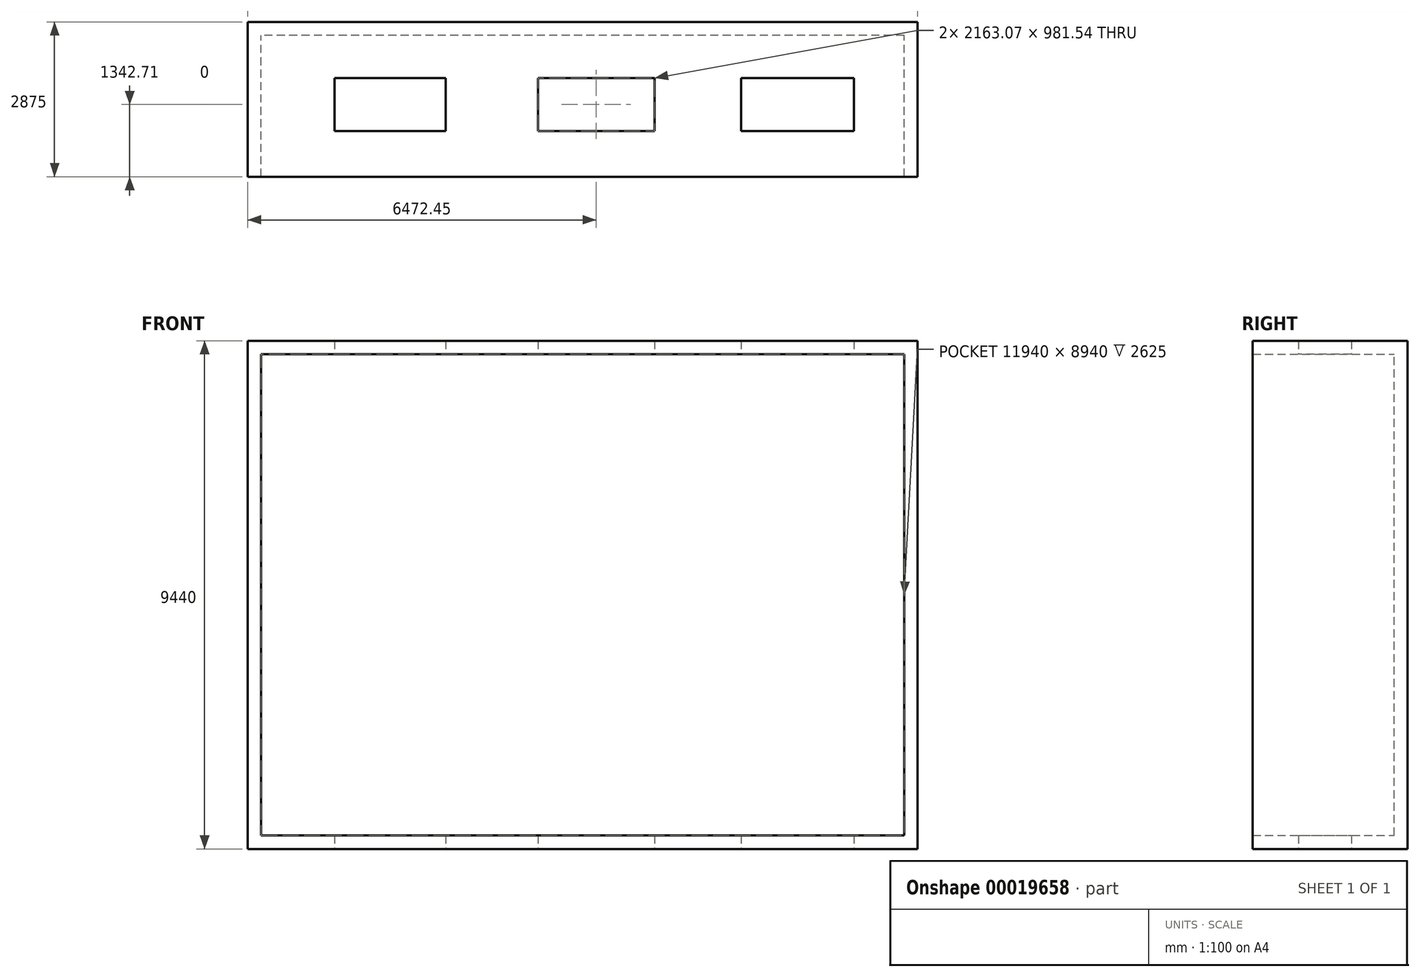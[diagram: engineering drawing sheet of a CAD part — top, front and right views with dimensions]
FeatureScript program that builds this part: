
annotation { "Feature Type Name" : "Feature", "Feature Type Description" : "" }
export const myFeature = defineFeature(function(context is Context, id is Id, definition is map)
    precondition{}
    {
        {
            var Q0;
            Q0=qCreatedBy(makeId("Front.planeOp"),FACE);
            var sketch = newSketch(context, id + "F0", { "sketchPlane" : qUnion([Q0])});
            skLineSegment(sketch, "E0.bottom", {"start": v(0, 0) * mm, "end": v(12440, 0) * mm});
            skLineSegment(sketch, "E0.top", {"start": v(0, 9440) * mm, "end": v(12440, 9440) * mm});
            skLineSegment(sketch, "E0.left", {"start": v(0, 0) * mm, "end": v(0, 9440) * mm});
            skLineSegment(sketch, "E0.right", {"start": v(12440, 0) * mm, "end": v(12440, 9440) * mm});
            skSolve(sketch);
        }
        {
            var Q0;
            Q0=makeQuery(id+"F0.imprint","IMPRINT",FACE,{"disambiguationData":[TD([[makeQuery(id+"F0.imprint","IMPRINT",EDGE,{"derivedFrom":sQuery(id+"F0.wireOp",EDGE,"E0.bottom")}),1.0]])]});
            extrude(context, id + "F1", {"entities" : qUnion([Q0]), "depth" : 250 * mm});
        }
        {
            var Q0;
            Q0=makeQuery(id+"F1.opExtrude","CAP_FACE",FACE,{"disambiguationData":[OSD([sQuery(id+"F0.wireOp",EDGE,"E0.bottom"),sQuery(id+"F0.wireOp",EDGE,"E0.top"),sQuery(id+"F0.wireOp",EDGE,"E0.left"),sQuery(id+"F0.wireOp",EDGE,"E0.right")])],"isStart":false});
            var sketch = newSketch(context, id + "F2", { "sketchPlane" : qUnion([Q0])});
            skLineSegment(sketch, "E1.0.0", {"start": v(0, 9440) * mm, "end": v(0, 0) * mm});
            skLineSegment(sketch, "E1.0.1", {"start": v(0, 0) * mm, "end": v(12440, 0) * mm});
            skLineSegment(sketch, "E1.0.2", {"start": v(12440, 0) * mm, "end": v(12440, 9440) * mm});
            skLineSegment(sketch, "E1.0.3", {"start": v(12440, 9440) * mm, "end": v(0, 9440) * mm});
            skLineSegment(sketch, "E2.0", {"start": v(12190, 9190) * mm, "end": v(250, 9190) * mm});
            skLineSegment(sketch, "E2.1", {"start": v(12190, 250) * mm, "end": v(12190, 9190) * mm});
            skLineSegment(sketch, "E2.2", {"start": v(250, 250) * mm, "end": v(12190, 250) * mm});
            skLineSegment(sketch, "E2.3", {"start": v(250, 9190) * mm, "end": v(250, 250) * mm});
            skSolve(sketch);
        }
        {
            var Q0;
            Q0=makeQuery(id+"F2.imprint","IMPRINT",FACE,{"disambiguationData":[TD([[makeQuery(id+"F2.imprint","IMPRINT",EDGE,{"derivedFrom":sQuery(id+"F2.wireOp",EDGE,"E1.0.0")}),-1.0]])]});
            extrude(context, id + "F3", {"entities" : qUnion([Q0]), "operationType" : NewBodyOperationType.ADD, "depth" : 2625 * mm});
        }
        {
            var Q0;
            Q0=makeQuery(id+"F3.boolean.opBoolean","MERGE",FACE,{"derivedFrom":[makeQuery(id+"F1.opExtrude","SWEPT_FACE",FACE,{"disambiguationData":[OSD([sQuery(id+"F0.wireOp",EDGE,"E0.bottom")])]}),makeQuery(id+"F3.opExtrude","SWEPT_FACE",FACE,{"disambiguationData":[OSD([sQuery(id+"F2.wireOp",EDGE,"E1.0.1")])]})]});
            var sketch = newSketch(context, id + "F4", { "sketchPlane" : qUnion([Q0])});
            skLineSegment(sketch, "E3.bottom", {"start": v(1614.22, 1041.52) * mm, "end": v(3676.65, 1041.52) * mm});
            skLineSegment(sketch, "E3.top", {"start": v(1614.22, 2023.06) * mm, "end": v(3676.65, 2023.06) * mm});
            skLineSegment(sketch, "E3.left", {"start": v(1614.22, 1041.52) * mm, "end": v(1614.22, 2023.06) * mm});
            skLineSegment(sketch, "E3.right", {"start": v(3676.65, 1041.52) * mm, "end": v(3676.65, 2023.06) * mm});
            skLineSegment(sketch, "E4.bottom", {"start": v(5390.92, 1041.52) * mm, "end": v(7553.99, 1041.52) * mm});
            skLineSegment(sketch, "E4.top", {"start": v(5390.92, 2023.06) * mm, "end": v(7553.99, 2023.06) * mm});
            skLineSegment(sketch, "E4.left", {"start": v(5390.92, 1041.52) * mm, "end": v(5390.92, 2023.06) * mm});
            skLineSegment(sketch, "E4.right", {"start": v(7553.99, 1041.52) * mm, "end": v(7553.99, 2023.06) * mm});
            skLineSegment(sketch, "E5.bottom", {"start": v(9161.17, 1041.52) * mm, "end": v(11260.6, 1041.52) * mm});
            skLineSegment(sketch, "E5.top", {"start": v(9161.17, 2023.06) * mm, "end": v(11260.6, 2023.06) * mm});
            skLineSegment(sketch, "E5.left", {"start": v(9161.17, 1041.52) * mm, "end": v(9161.17, 2023.06) * mm});
            skLineSegment(sketch, "E5.right", {"start": v(11260.6, 1041.52) * mm, "end": v(11260.6, 2023.06) * mm});
            skSolve(sketch);
        }
        {
            var Q0;
            Q0 = qSketchRegion(id + "F4", true);
            extrude(context, id + "F5", {"entities" : qUnion([Q0]), "operationType" : NewBodyOperationType.REMOVE, "oppositeDirection" : true, "depth" : 11085.94 * mm});
        }
    });
